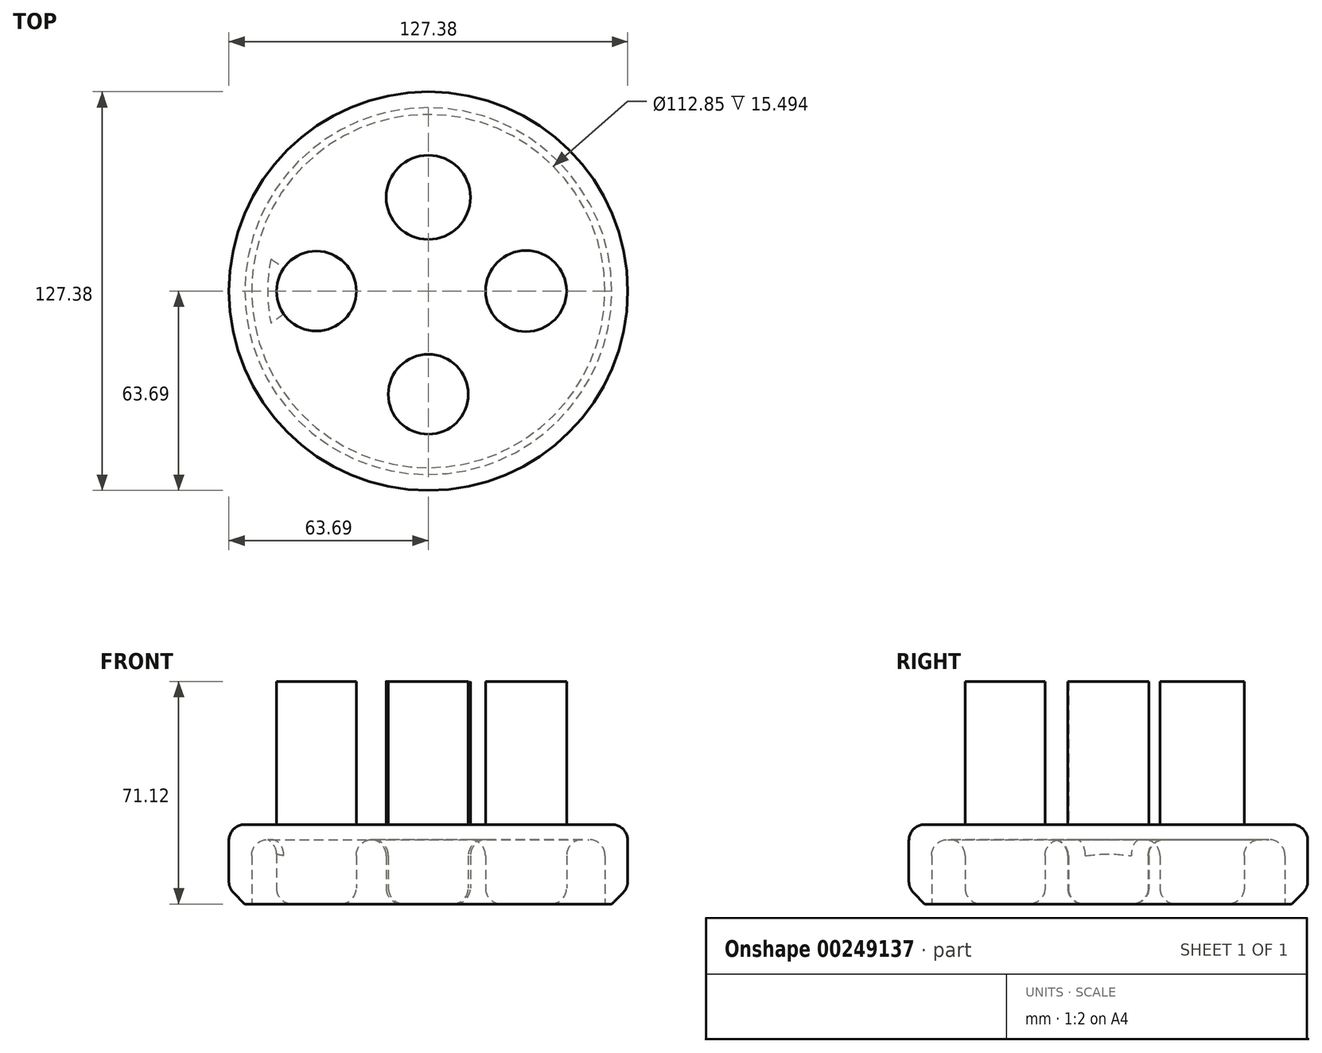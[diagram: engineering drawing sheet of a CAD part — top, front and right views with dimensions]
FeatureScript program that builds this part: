
annotation { "Feature Type Name" : "Feature", "Feature Type Description" : "" }
export const myFeature = defineFeature(function(context is Context, id is Id, definition is map)
    precondition{}
    {
        {
            var Q0;
            Q0=qCreatedBy(makeId("Top.planeOp"),FACE);
            var sketch = newSketch(context, id + "F0", { "sketchPlane" : qUnion([Q0])});
            skCircle(sketch, "E0", {"center": v(0, 0) * mm, "radius": 63.69 * mm});
            skSolve(sketch);
        }
        {
            var Q0;
            Q0=makeQuery(id+"F0.imprint","IMPRINT",FACE,{"disambiguationData":[TD([[makeQuery(id+"F0.imprint","IMPRINT",EDGE,{"derivedFrom":sQuery(id+"F0.wireOp",EDGE,"E0")}),1.0]])]});
            extrude(context, id + "F1", {"entities" : qUnion([Q0]), "depth" : 25.4 * mm});
        }
        {
            var Q0;
            Q0=qCreatedBy(makeId("Top.planeOp"),FACE);
            var sketch = newSketch(context, id + "F2", { "sketchPlane" : qUnion([Q0])});
            skCircle(sketch, "E1", {"center": v(0, 0) * mm, "radius": 56.43 * mm});
            skSolve(sketch);
        }
        {
            var Q0;
            Q0=makeQuery(id+"F2.imprint","IMPRINT",FACE,{"disambiguationData":[TD([[makeQuery(id+"F2.imprint","IMPRINT",EDGE,{"derivedFrom":sQuery(id+"F2.wireOp",EDGE,"E1")}),1.0]])]});
            extrude(context, id + "F3", {"entities" : qUnion([Q0]), "operationType" : NewBodyOperationType.REMOVE, "depth" : 20.57 * mm});
        }
        {
            var Q0;
            Q0=qCreatedBy(makeId("Top.planeOp"),FACE);
            var sketch = newSketch(context, id + "F4", { "sketchPlane" : qUnion([Q0])});
            skCircle(sketch, "E2", {"center": v(0, -32.97) * mm, "radius": 12.77 * mm});
            skCircle(sketch, "E3", {"center": v(31.2, 0) * mm, "radius": 12.95 * mm});
            skCircle(sketch, "E4", {"center": v(-35.75, 0) * mm, "radius": 12.74 * mm});
            skCircle(sketch, "E5", {"center": v(0, 29.95) * mm, "radius": 13.45 * mm});
            skSolve(sketch);
        }
        {
            var Q0;
            Q0=makeQuery(id+"F4.imprint","IMPRINT",FACE,{"disambiguationData":[TD([[makeQuery(id+"F4.imprint","IMPRINT",EDGE,{"derivedFrom":sQuery(id+"F4.wireOp",EDGE,"E5")}),1.0]])]});
            var Q1;
            Q1=makeQuery(id+"F4.imprint","IMPRINT",FACE,{"disambiguationData":[TD([[makeQuery(id+"F4.imprint","IMPRINT",EDGE,{"derivedFrom":sQuery(id+"F4.wireOp",EDGE,"E4")}),1.0]])]});
            var Q2;
            Q2=makeQuery(id+"F4.imprint","IMPRINT",FACE,{"disambiguationData":[TD([[makeQuery(id+"F4.imprint","IMPRINT",EDGE,{"derivedFrom":sQuery(id+"F4.wireOp",EDGE,"E2")}),1.0]])]});
            var Q3;
            Q3=makeQuery(id+"F4.imprint","IMPRINT",FACE,{"disambiguationData":[TD([[makeQuery(id+"F4.imprint","IMPRINT",EDGE,{"derivedFrom":sQuery(id+"F4.wireOp",EDGE,"E3")}),1.0]])]});
            extrude(context, id + "F5", {"entities" : qUnion([Q0, Q1, Q2, Q3]), "operationType" : NewBodyOperationType.ADD, "depth" : 71.12 * mm});
        }
        {
            var Q0;
            Q0=makeQuery(id+"F1.opExtrude","CAP_EDGE",EDGE,{"disambiguationData":[OSD([sQuery(id+"F0.wireOp",EDGE,"E0")])],"isStart":true});
            chamfer(context, id + "F6", {"entities" : qUnion([Q0]), "width" : 5.08 * mm, "tangentPropagation" : true});
        }
        {
            var Q0;
            Q0=makeQuery(id+"F3.boolean.opBoolean","COPY",EDGE,{"derivedFrom":makeQuery(id+"F3.opExtrude","CAP_EDGE",EDGE,{"disambiguationData":[OSD([sQuery(id+"F2.wireOp",EDGE,"E1")])],"isStart":false})});
            fillet(context, id + "F7", {"entities" : qUnion([Q0]), "radius" : 5.08 * mm, "tangentPropagation" : true, "allowEdgeOverflow" : false});
        }
        {
            var Q0;
            Q0=makeQuery(id+"F1.opExtrude","CAP_EDGE",EDGE,{"disambiguationData":[OSD([sQuery(id+"F0.wireOp",EDGE,"E0")])],"isStart":false});
            var Q1;
            {var subQ0=sQuery(id+"F0.wireOp",EDGE,"E0");Q1=makeQuery(id+"F6.opChamfer","BLEND_EDGE",EDGE,{"blendedFrom":[makeQuery(id+"F1.opExtrude","CAP_EDGE",EDGE,{"disambiguationData":[OSD([subQ0])],"isStart":true}),makeQuery(id+"F1.opExtrude","SWEPT_FACE",FACE,{"disambiguationData":[OSD([subQ0])]})],"blendedInto":[makeQuery(id+"F1.opExtrude","SWEPT_FACE",FACE,{"disambiguationData":[OSD([subQ0])]})]});}
            fillet(context, id + "F8", {"entities" : qUnion([Q0, Q1]), "radius" : 5.08 * mm, "tangentPropagation" : true, "allowEdgeOverflow" : false});
        }
        {
            var Q0;
            Q0=makeQuery(id+"F5.opExtrude","CAP_EDGE",EDGE,{"disambiguationData":[OSD([sQuery(id+"F4.wireOp",EDGE,"E2")])],"isStart":true});
            var Q1;
            Q1=makeQuery(id+"Frx5xBcAF7iZSzG_1.opExtrude","CAP_EDGE",EDGE,{"disambiguationData":[OSD([sQuery(id+"F6ZxOCtCPwgK2Ix_1.wireOp",EDGE,"X6tEaaN2-yeBg-zcCz-Pxd0-pjcRoaH9VAZi")])],"isStart":true});
            var Q2;
            Q2=makeQuery(id+"F5.opExtrude","CAP_EDGE",EDGE,{"disambiguationData":[OSD([sQuery(id+"F4.wireOp",EDGE,"E3")])],"isStart":true});
            var Q3;
            Q3=makeQuery(id+"F5.opExtrude","CAP_EDGE",EDGE,{"disambiguationData":[OSD([sQuery(id+"F4.wireOp",EDGE,"E5")])],"isStart":true});
            var Q4;
            Q4=makeQuery(id+"F5.opExtrude","CAP_EDGE",EDGE,{"disambiguationData":[OSD([sQuery(id+"F4.wireOp",EDGE,"E4")])],"isStart":true});
            fillet(context, id + "F9", {"entities" : qUnion([Q0, Q1, Q2, Q3, Q4]), "radius" : 5.08 * mm, "tangentPropagation" : true, "allowEdgeOverflow" : false});
        }
        {
            var Q0;
            Q0=makeQuery(id+"F5.boolean.opBoolean","INTERSECT",EDGE,{"derivedFrom":[makeQuery(id+"F3.boolean.opBoolean","COPY",FACE,{"derivedFrom":makeQuery(id+"F3.opExtrude","CAP_FACE",FACE,{"disambiguationData":[OSD([sQuery(id+"F2.wireOp",EDGE,"E1")])],"isStart":false})}),makeQuery(id+"F5.opExtrude","SWEPT_FACE",FACE,{"disambiguationData":[OSD([sQuery(id+"F4.wireOp",EDGE,"E2")])]})]});
            var Q1;
            Q1=makeQuery(id+"Frx5xBcAF7iZSzG_1.boolean.opBoolean","INTERSECT",EDGE,{"derivedFrom":[makeQuery(id+"F3.boolean.opBoolean","COPY",FACE,{"derivedFrom":makeQuery(id+"F3.opExtrude","CAP_FACE",FACE,{"disambiguationData":[OSD([sQuery(id+"F2.wireOp",EDGE,"E1")])],"isStart":false})}),makeQuery(id+"Frx5xBcAF7iZSzG_1.opExtrude","SWEPT_FACE",FACE,{"disambiguationData":[OSD([sQuery(id+"F6ZxOCtCPwgK2Ix_1.wireOp",EDGE,"X6tEaaN2-yeBg-zcCz-Pxd0-pjcRoaH9VAZi")])]})]});
            var Q2;
            Q2=makeQuery(id+"F5.boolean.opBoolean","INTERSECT",EDGE,{"derivedFrom":[makeQuery(id+"F3.boolean.opBoolean","COPY",FACE,{"derivedFrom":makeQuery(id+"F3.opExtrude","CAP_FACE",FACE,{"disambiguationData":[OSD([sQuery(id+"F2.wireOp",EDGE,"E1")])],"isStart":false})}),makeQuery(id+"F5.opExtrude","SWEPT_FACE",FACE,{"disambiguationData":[OSD([sQuery(id+"F4.wireOp",EDGE,"E3")])]})]});
            var Q3;
            Q3=makeQuery(id+"F5.boolean.opBoolean","INTERSECT",EDGE,{"derivedFrom":[makeQuery(id+"F3.boolean.opBoolean","COPY",FACE,{"derivedFrom":makeQuery(id+"F3.opExtrude","CAP_FACE",FACE,{"disambiguationData":[OSD([sQuery(id+"F2.wireOp",EDGE,"E1")])],"isStart":false})}),makeQuery(id+"F5.opExtrude","SWEPT_FACE",FACE,{"disambiguationData":[OSD([sQuery(id+"F4.wireOp",EDGE,"E5")])]})]});
            var Q4;
            Q4=makeQuery(id+"F5.boolean.opBoolean","INTERSECT",EDGE,{"derivedFrom":[makeQuery(id+"F3.boolean.opBoolean","COPY",FACE,{"derivedFrom":makeQuery(id+"F3.opExtrude","CAP_FACE",FACE,{"disambiguationData":[OSD([sQuery(id+"F2.wireOp",EDGE,"E1")])],"isStart":false})}),makeQuery(id+"F5.opExtrude","SWEPT_FACE",FACE,{"disambiguationData":[OSD([sQuery(id+"F4.wireOp",EDGE,"E4")])]})]});
            fillet(context, id + "F10", {"entities" : qUnion([Q0, Q1, Q2, Q3, Q4]), "radius" : 5.08 * mm, "tangentPropagation" : true, "allowEdgeOverflow" : false});
        }
    });
